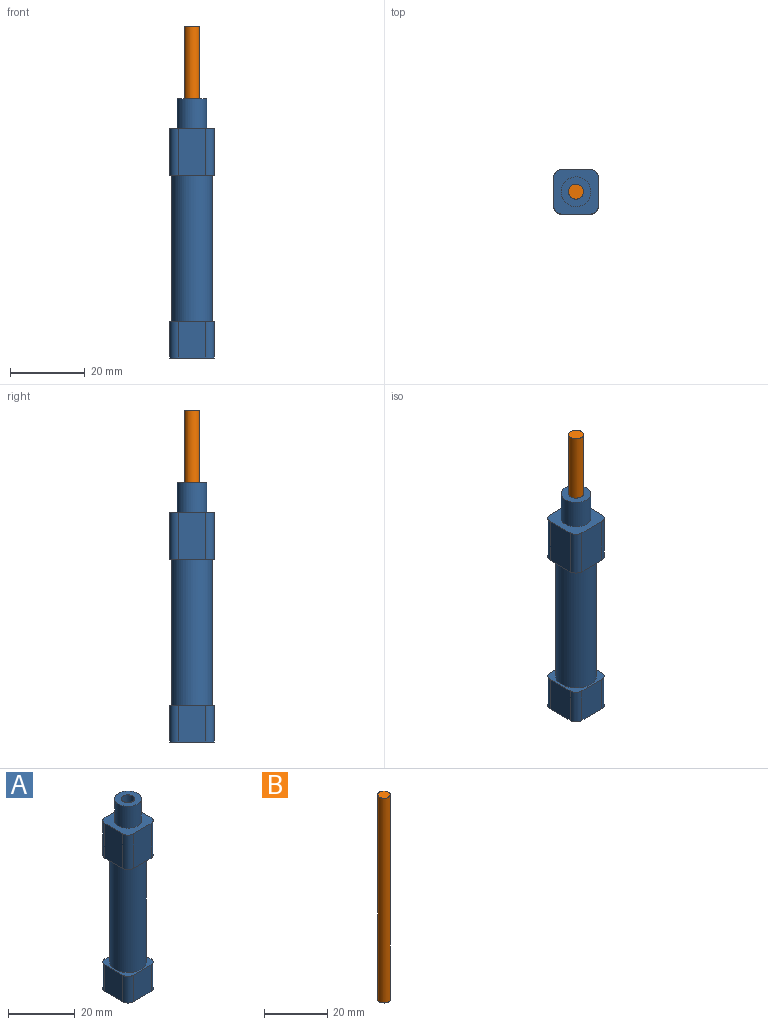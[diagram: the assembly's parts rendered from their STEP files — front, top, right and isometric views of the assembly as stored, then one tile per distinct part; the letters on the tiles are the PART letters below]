
ASSEMBLY  parts=2 mates=1
PART A: 25 faces, bbox 12x12x69.6 mm
  f0: plane 9.7x7.5mm, normal (1,0,0), area 72.8mm2, adj f1,f7,f8,f9
  f1: cylinder r=2.25mm len=9.7mm, axis (0,0,-1), area 34.3mm2, adj f0,f2,f8,f9
  f2: plane 9.7x7.5mm, normal (0,1,0), area 72.8mm2, adj f1,f3,f8,f9
  f3: cylinder r=2.25mm len=9.7mm, axis (0,0,-1), area 34.3mm2, adj f2,f4,f8,f9
  f4: plane 9.7x7.5mm, normal (-1,0,0), area 72.8mm2, adj f3,f5,f8,f9
  f5: cylinder r=2.25mm len=9.7mm, axis (0,0,-1), area 34.3mm2, adj f4,f6,f8,f9
  f6: plane 9.7x7.5mm, normal (0,-1,0), area 72.8mm2, adj f5,f7,f8,f9
  f7: cylinder r=2.25mm len=9.7mm, axis (0,0,-1), area 34.3mm2, adj f0,f6,f8,f9
  f8: plane 12x12mm, normal (0,0,1), area 44.6mm2, adj f0,f1,f2,f3,f4,f5,f6,f7
  f9: plane 12x12mm, normal (0,0,-1), area 139.7mm2, adj f0,f1,f2,f3,f4,f5,f6,f7
  f10: cylinder r=5.5mm len=39.2mm, axis (0,0,-1), area 1354.7mm2, adj f8,f20
  f11: plane 12.7x7.5mm, normal (1,0,0), area 95.2mm2, adj f12,f18,f19,f20
  f12: cylinder r=2.25mm len=12.7mm, axis (0,0,-1), area 44.9mm2, adj f11,f13,f19,f20
  f13: plane 12.7x7.5mm, normal (0,1,0), area 95.2mm2, adj f12,f14,f19,f20
  f14: cylinder r=2.25mm len=12.7mm, axis (0,0,-1), area 44.9mm2, adj f13,f15,f19,f20
  f15: plane 12.7x7.5mm, normal (-1,0,0), area 95.2mm2, adj f14,f16,f19,f20
  f16: cylinder r=2.25mm len=12.7mm, axis (0,0,-1), area 44.9mm2, adj f15,f17,f19,f20
  f17: plane 12.7x7.5mm, normal (0,-1,0), area 95.2mm2, adj f16,f18,f19,f20
  f18: cylinder r=2.25mm len=12.7mm, axis (0,0,-1), area 44.9mm2, adj f11,f17,f19,f20
  f19: plane 12x12mm, normal (0,0,1), area 89.4mm2, adj f11,f12,f13,f14,f15,f16,f17,f18
  f20: plane 12x12mm, normal (0,0,-1), area 44.6mm2, adj f10,f11,f12,f13,f14,f15,f16,f17
  f21: cylinder r=4mm len=8mm, axis (0,0,-1), area 201.1mm2, adj f19,f22
  f22: plane 8x8mm, normal (0,0,1), area 37.7mm2, adj f21,f23
  f23: cylinder r=2mm len=60mm, axis (0,0,1), area 754mm2, adj f22,f24
  f24: plane 4x4mm, normal (0,0,1), area 12.6mm2, adj f23
PART B: 3 faces, bbox 4x4x79.5 mm
  f0: cylinder r=2mm len=79.5mm, axis (0,0,-1), area 999mm2, adj f1,f2
  f1: plane 4x4mm, normal (0,0,1), area 12.6mm2, adj f0
  f2: plane 4x4mm, normal (0,0,-1), area 12.6mm2, adj f0
PLACE A at identity
PLACE B rot(axis=(0,0,1),180deg) t=(0,0,0)mm
MATE slider B.f0 <-> A.f23  axis (0,0,-1) through (0,0,9.6)mm
